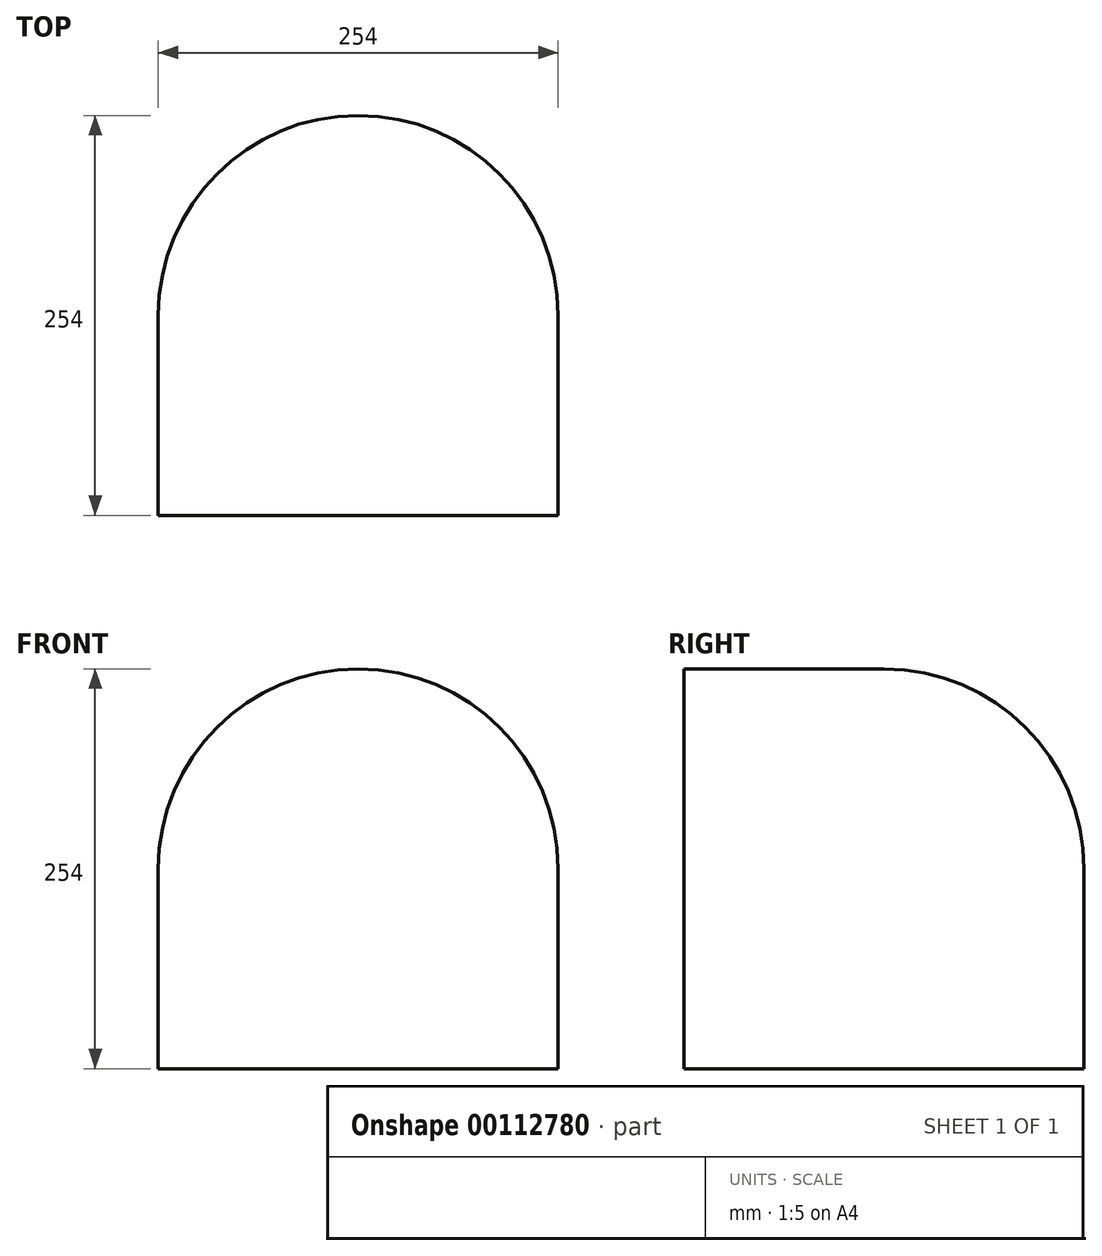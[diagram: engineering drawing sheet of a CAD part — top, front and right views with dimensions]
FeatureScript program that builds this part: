
annotation { "Feature Type Name" : "Feature", "Feature Type Description" : "" }
export const myFeature = defineFeature(function(context is Context, id is Id, definition is map)
    precondition{}
    {
        {
            var Q0;
            Q0=qCreatedBy(makeId("Top.planeOp"),FACE);
            var sketch = newSketch(context, id + "F0", { "sketchPlane" : qUnion([Q0])});
            skLineSegment(sketch, "E0.bottom", {"start": v(-76.2, 177.8) * mm, "end": v(177.8, 177.8) * mm});
            skLineSegment(sketch, "E0.top", {"start": v(-76.2, -76.2) * mm, "end": v(177.8, -76.2) * mm});
            skLineSegment(sketch, "E0.left", {"start": v(-76.2, 177.8) * mm, "end": v(-76.2, -76.2) * mm});
            skLineSegment(sketch, "E0.right", {"start": v(177.8, 177.8) * mm, "end": v(177.8, -76.2) * mm});
            skSolve(sketch);
        }
        {
            var Q0;
            Q0=makeQuery(id+"F0.imprint","IMPRINT",FACE,{"disambiguationData":[TD([[makeQuery(id+"F0.imprint","IMPRINT",EDGE,{"derivedFrom":sQuery(id+"F0.wireOp",EDGE,"E0.bottom")}),-1.0]])]});
            extrude(context, id + "F1", {"entities" : qUnion([Q0]), "depth" : 254 * mm});
        }
        {
            var Q0;
            Q0=makeQuery(id+"F1.opExtrude","CAP_EDGE",EDGE,{"disambiguationData":[OSD([sQuery(id+"F0.wireOp",EDGE,"E0.left")])],"isStart":false});
            var Q1;
            Q1=makeQuery(id+"F1.opExtrude","CAP_EDGE",EDGE,{"disambiguationData":[OSD([sQuery(id+"F0.wireOp",EDGE,"E0.right")])],"isStart":false});
            fillet(context, id + "F2", {"entities" : qUnion([Q0, Q1]), "radius" : 127 * mm, "tangentPropagation" : true, "allowEdgeOverflow" : false});
        }
        {
            var Q0;
            Q0=makeQuery(id+"F2.opFillet","BLEND_EDGE",EDGE,{"blendedFrom":[makeQuery(id+"F1.opExtrude","CAP_EDGE",EDGE,{"disambiguationData":[OSD([sQuery(id+"F0.wireOp",EDGE,"E0.right")])],"isStart":false}),makeQuery(id+"F1.opExtrude","SWEPT_FACE",FACE,{"disambiguationData":[OSD([sQuery(id+"F0.wireOp",EDGE,"E0.bottom")])]})],"blendedInto":[makeQuery(id+"F1.opExtrude","SWEPT_FACE",FACE,{"disambiguationData":[OSD([sQuery(id+"F0.wireOp",EDGE,"E0.bottom")])]})]});
            var Q1;
            Q1=makeQuery(id+"F1.opExtrude","SWEPT_EDGE",EDGE,{"disambiguationData":[OSD([sQuery(id+"F0.wireOp",EDGE,"E0.bottom"),sQuery(id+"F0.wireOp",EDGE,"E0.right")])]});
            var Q2;
            Q2=makeQuery(id+"F1.opExtrude","SWEPT_EDGE",EDGE,{"disambiguationData":[OSD([sQuery(id+"F0.wireOp",EDGE,"E0.bottom"),sQuery(id+"F0.wireOp",EDGE,"E0.left")])]});
            var Q3;
            Q3=makeQuery(id+"F2.opFillet","BLEND_EDGE",EDGE,{"blendedFrom":[makeQuery(id+"F1.opExtrude","CAP_EDGE",EDGE,{"disambiguationData":[OSD([sQuery(id+"F0.wireOp",EDGE,"E0.right")])],"isStart":false}),makeQuery(id+"F1.opExtrude","SWEPT_FACE",FACE,{"disambiguationData":[OSD([sQuery(id+"F0.wireOp",EDGE,"E0.top")])]})],"blendedInto":[makeQuery(id+"F1.opExtrude","SWEPT_FACE",FACE,{"disambiguationData":[OSD([sQuery(id+"F0.wireOp",EDGE,"E0.top")])]})]});
            fillet(context, id + "F3", {"entities" : qUnion([Q0, Q1, Q2, Q3]), "radius" : 127 * mm, "tangentPropagation" : true, "allowEdgeOverflow" : false});
        }
    });
